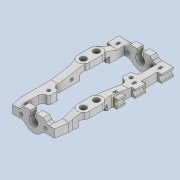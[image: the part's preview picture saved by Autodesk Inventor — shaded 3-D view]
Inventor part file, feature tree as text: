
AUTODESK INVENTOR PART (.ipt)
format: ipt  version: 2020 (Build 240168000, 168)  size: 996,352 bytes
history: native  units: mm
features: projected_geometry x29, sketch x26, extrude x24, thicken_offset x10, fillet x9, chamfer x7, other x5, plane x3, reference x3, hole x2
ambient origin geometry x8: Origin, YZ Plane, XZ Plane, XY Plane, X Axis, Y Axis, Z Axis, Center Point
bodies: Solid1 (feature_tree)
feature tree (118):
  extrude  "Extrusion1"  Depth=10.0mm
  plane  "Work Plane1"
  extrude  "Extrusion2"  Depth=2.0mm TaperAngle=0.0deg
  extrude  "Extrusion3"  Depth=10.0mm
  extrude  "Extrusion4"  Depth=2.0mm TaperAngle=0.0deg
  hole  "Hole1"  [1 undecoded]
  thicken_offset  "Thicken1"
  thicken_offset  "Thicken2"
  thicken_offset  "Thicken3"
  thicken_offset  "Thicken4"
  extrude  "Extrusion5"  Depth=54.0mm
  extrude  "Extrusion6"  Depth=2.0mm
  extrude  "Extrusion8"  Depth=6.0mm
  extrude  "Extrusion9"  Depth=3.5mm
  extrude  "Extrusion11"  Depth=3.5mm
  hole  "Hole2"  [1 undecoded]
  extrude  "Extrusion15"  Depth=3.5mm
  extrude  "Extrusion16"  Depth=3.5mm
  chamfer  "Chamfer1"  Distance=2.0mm
  chamfer  "Chamfer2"  Distance=3.25mm
  chamfer  "Chamfer3"  Distance=6.5mm
  chamfer  "Chamfer4"  Distance=6.0mm
  fillet  "Fillet4"  Radius=2.0mm
  fillet  "Fillet5"  Radius=7.0mm
  chamfer  "Chamfer5"  Distance=3.0mm
  fillet  "Fillet6"  Radius=3.0mm
  extrude  "Extrusion17"  Depth=3.0mm
  plane  "Work Plane3"
  extrude  "Extrusion18"  Depth=3.0mm TaperAngle=0.0deg
  plane  "Work Plane4"
  extrude  "Extrusion19"  Depth=6.5mm
  extrude  "Extrusion20"  Depth=10.0mm
  extrude  "Extrusion21"  Depth=3.0mm TaperAngle=0.0deg
  extrude  "Extrusion22"  Depth=6.0mm
  thicken_offset  "Thicken9"
  thicken_offset  "Thicken10"
  thicken_offset  "Thicken11"
  thicken_offset  "Thicken12"
  extrude  "Extrusion23"  Depth=2.0mm TaperAngle=0.0deg
  fillet  "Fillet11"  Radius=6.0mm
  extrude  "Extrusion24"  Depth=2.0mm TaperAngle=0.0deg
  thicken_offset  "Thicken13"
  thicken_offset  "Thicken14"
  chamfer  "Chamfer7"  Distance=12.0mm Angle=30.0deg
  chamfer  "Chamfer8"  Distance=5.0mm Angle=30.0deg
  fillet  "Fillet12"  Radius=12.0mm
  fillet  "Fillet13"  Radius=5.0mm
  fillet  "Fillet14"  Radius=1.0mm
  extrude  "Extrusion26"  Depth=10.0mm
  extrude  "Extrusion27"  Depth=1.0mm TaperAngle=30.0deg
  extrude  "Extrusion28"  Depth=10.0mm
  extrude  "Extrusion29"  Depth=10.0mm
  fillet  "Fillet15"  Radius=2.0mm
  fillet  "Fillet16"  Radius=4.0mm
  extrude  "Extrusion30"  Depth=5.0mm TaperAngle=0.0deg
  sketch  "Sketch1"  dims[d0=10.0mm d1=4.0mm]
  sketch  "Sketch2"  dims[d2=30.0mm d3=2.0mm d4=0.0mm]
  sketch  "Sketch3"  dims[d5=10.0mm d6=4.0mm]
  projected_geometry  "Projected Loop1"
  projected_geometry  "Projected Loop2"
  projected_geometry  "Projected Loop3"
  projected_geometry  "Projected Loop4"
  sketch  "Sketch4"  dims[d7=30.0mm d8=2.0mm d9=0.0mm]
  sketch  "Sketch5"  dims[d10=3.0mm d11=54.0mm]
  sketch  "Sketch6"  dims[d12=3.0mm d13=54.0mm]
  projected_geometry  "Projected Loop5"
  reference  "Reference1"
  reference  "Reference2"
  sketch  "Sketch7"  dims[d14=2.0mm d15=0.0mm d16=4.5mm]
  projected_geometry  "Projected Loop6"
  reference  "Reference3"
  sketch  "Sketch9"  dims[d17=2.0mm d18=0.0mm d19=6.0mm]
  projected_geometry  "Projected Loop9"
  sketch  "Sketch10"  dims[d20=6.0mm]
  projected_geometry  "Projected Loop10"
  sketch  "Sketch12"  dims[d21=1.6mm d22=6.0mm d23=4.0mm d24=2.0mm d25=90.0deg d26=100.0mm d27=0.0mm d28=3.5mm]
  projected_geometry  "Projected Loop13"
  sketch  "Sketch13"  dims[d29=3.5mm d30=3.5mm]
  projected_geometry  "Projected Loop14"
  sketch  "Sketch18"  dims[d31=3.5mm d32=3.5mm]
  projected_geometry  "Projected Loop20"
  sketch  "Sketch19"  dims[d33=3.5mm d34=3.5mm]
  projected_geometry  "Projected Loop21"
  sketch  "Sketch20"  dims[d35=3.5mm d36=7.5mm]
  projected_geometry  "Projected Loop22"
  sketch  "Sketch21"  dims[d37=9.0mm]
  projected_geometry  "Projected Loop23"
  sketch  "Sketch22"  dims[d38=3.0mm]
  projected_geometry  "Projected Loop24"
  sketch  "Sketch23"  dims[d39=3.25mm]
  projected_geometry  "Projected Loop25"
  sketch  "Sketch24"  dims[d40=3.25mm]
  projected_geometry  "Projected Loop26"
  sketch  "Sketch25"  dims[d41=6.0mm]
  projected_geometry  "Projected Loop27"
  sketch  "Sketch26"  dims[d42=6.0mm]
  projected_geometry  "Projected Loop28"
  projected_geometry  "Projected Loop29"
  sketch  "Sketch27"  dims[d43=2.0mm]
  projected_geometry  "Projected Loop30"
  projected_geometry  "Projected Loop31"
  sketch  "Sketch29"  dims[d44=6.5mm]
  projected_geometry  "Projected Loop33"
  sketch  "Sketch30"  dims[d45=6.0mm d46=2.0mm d47=0.0mm]
  projected_geometry  "Projected Loop34"
  projected_geometry  "Projected Loop35"
  sketch  "Sketch31"  dims[d48=7.5mm]
  projected_geometry  "Projected Loop36"
  sketch  "Sketch32"  dims[d49=9.0mm]
  projected_geometry  "Projected Loop37"
  projected_geometry  "Projected Loop38"
  sketch  "Sketch34"  dims[d50=2.0mm d51=3.25mm d52=6.5mm d53=6.0mm d54=2.0mm d55=0.0mm d60=7.0mm d61=3.0mm d62=0.0mm d66=3.0mm d67=3.0mm d68=3.0mm d69=0.0mm d76=6.5mm d77=7.0mm d78=3.0mm d79=0.0mm d80=3.0mm d81=6.0mm d82=4.0mm d83=2.0mm d84=90.0deg d85=100.0mm d86=0.0mm d107=6.0mm d108=2.0mm d109=0.0mm d110=6.0mm d111=2.0mm d112=0.0mm d113=12.0mm d114=2.0mm d115=30.0deg d116=5.0mm d117=2.0mm d118=30.0deg d119=12.0mm d120=2.0mm d121=30.0deg d122=5.0mm d123=2.0mm d124=30.0deg d125=1.0mm d126=8.0mm d127=1.0mm d128=2.0mm d129=30.0deg d130=0.5mm d135=2.5mm d136=2.0mm d137=4.0mm d138=5.0mm d139=0.0mm d140=8.0mm d141=5.0mm d142=0.0mm d143=9.0mm d144=4.0mm d145=0.0mm d146=2.5mm d147=2.0mm d148=4.0mm d149=5.0mm d150=0.0mm d154=3.0mm d155=2.0mm d156=3.0mm d157=2.0mm d158=3.0mm d159=2.0mm d160=0.5mm d161=1.0mm d162=0.5mm d163=1.0mm d164=0.5mm d165=1.0mm d166=8.0mm d167=0.0mm d168=3.0mm d169=0.5mm d170=1.0mm d171=8.0mm d172=0.0mm d173=0.5mm d174=0.5mm d175=0.5mm d176=0.5mm d177=0.5mm d178=0.5mm d179=0.5mm d180=0.5mm d181=12.0mm d182=1.5mm d183=3.0mm d184=5.0mm d185=12.0mm d186=1.5mm d187=3.0mm d188=5.0mm d189=8.0mm d190=0.0mm d191=2.0mm d192=2.5mm d193=1.6mm d194=2.5mm d195=1.6mm d196=8.0mm d197=0.0mm d198=1.0mm d199=1.0mm d200=1.0mm d201=1.0mm d202=1.0mm d203=6.0mm d204=30.0deg d205=1.0mm d206=6.0mm d207=30.0deg d208=4.0mm d209=4.0mm d210=1.0mm d215=6.0mm d216=3.0mm d217=10.0mm d218=0.0mm d219=10.0mm d220=0.0mm d221=2.0mm d222=2.0mm d223=10.0mm d224=0.0mm d225=10.0mm d226=0.0mm d227=2.0mm d228=3.0mm d230=2.0mm d231=0.25mm d232=1.5mm d233=10.0mm d234=0.0mm]
  projected_geometry  "Projected Loop40"
  parser-record x1  (decoder bookkeeping rows leaked as tree rows — omitted from the tree; the rows remain in map.json)
  other  "tip2_ass_t1.iam"
  other  "cab_coil_1:1"
  other  "cab_coil_1:2"
  other  "bearing_3_6_2:1"
note: 2 required parameter values undecoded (feature->parameter linkage not recoverable at this tier; creation-order binding heuristic only, values carry confidence <= 0.55)
note: 1 file-system path scrubbed to <path> (originals preserved in map.json)
